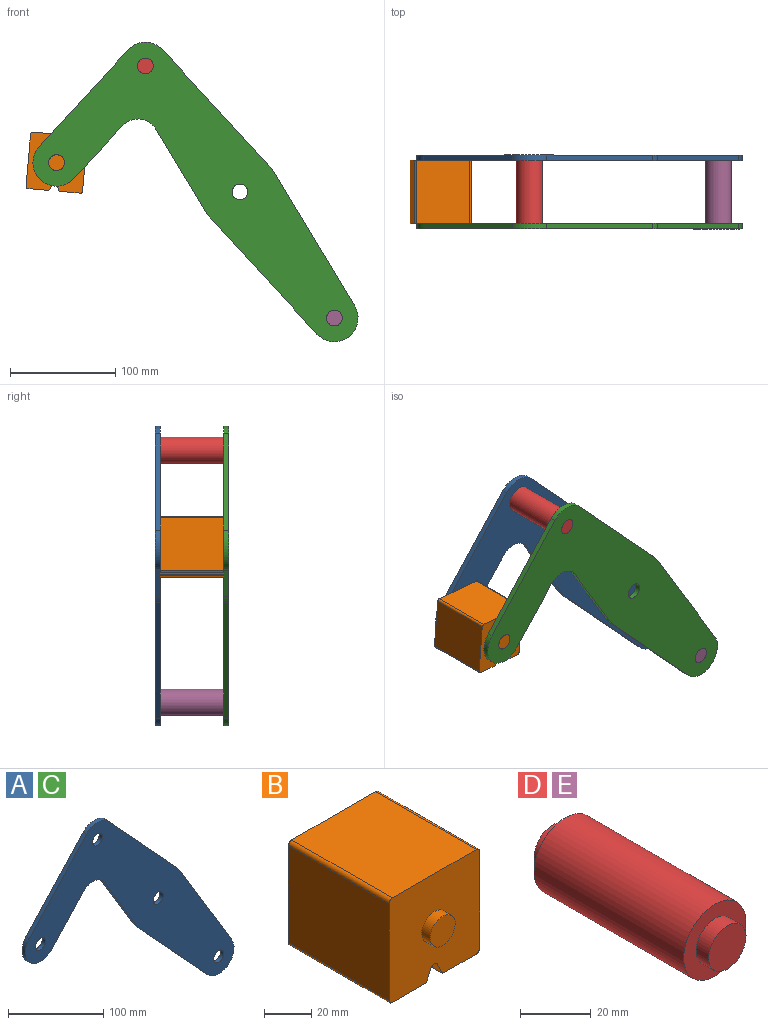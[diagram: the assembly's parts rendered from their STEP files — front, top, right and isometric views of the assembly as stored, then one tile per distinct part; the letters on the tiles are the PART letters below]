
ASSEMBLY  parts=5 mates=3
PART A: 18 faces, bbox 309.5x5x285.1 mm
  f0: cylinder r=22.5mm len=39.07mm, axis (0,1,0), area 353.4mm2, adj f1,f13,f16,f17
  f1: plane 50.28x46.21mm, normal (0.74,0,-0.68), area 341.4mm2, adj f0,f2,f16,f17
  f2: cylinder r=20mm len=31.85mm, axis (0,1,0), area 185.5mm2, adj f1,f3,f16,f17
  f3: plane 79.23x47.81mm, normal (-0.86,0,-0.52), area 462.7mm2, adj f2,f4,f16,f17
  f4: cylinder r=37.5mm len=6mm, axis (0,1,0), area 37.6mm2, adj f3,f5,f16,f17
  f5: plane 109.88x101mm, normal (-0.74,0,-0.68), area 746.2mm2, adj f4,f6,f16,f17
  f6: cylinder r=22.5mm len=39.07mm, axis (0,1,0), area 330.9mm2, adj f5,f7,f16,f17
  f7: plane 127.78x77.11mm, normal (0.86,0,0.52), area 746.2mm2, adj f6,f8,f16,f17
  f8: cylinder r=37.5mm len=6mm, axis (0,1,0), area 37.6mm2, adj f7,f9,f16,f17
  f9: plane 109.88x101mm, normal (0.74,0,0.68), area 746.2mm2, adj f8,f10,f16,f17
  f10: cylinder r=22.5mm len=33.13mm, axis (0,1,0), area 186.2mm2, adj f9,f13,f16,f17
  f11: cylinder r=7.5mm len=15mm, axis (0,1,0), area 235.6mm2, adj f16,f17
  f12: cylinder r=7.5mm len=15mm, axis (0,1,0), area 235.6mm2, adj f16,f17
  f13: plane 92.03x84.59mm, normal (-0.74,0,0.68), area 625mm2, adj f0,f10,f16,f17
  f14: cylinder r=7.5mm len=15mm, axis (0,1,0), area 235.6mm2, adj f16,f17
  f15: cylinder r=7.5mm len=15mm, axis (0,1,0), area 235.6mm2, adj f16,f17
  f16: plane 309.5x285.07mm, normal (0,-1,0), area 24555.4mm2, adj f0,f1,f2,f3,f4,f5,f6,f7
  f17: plane 309.5x285.07mm, normal (0,1,0), area 24555.4mm2, adj f0,f1,f2,f3,f4,f5,f6,f7
PART B: 18 faces, bbox 54x70x54 mm
  f0: plane 60x50.01mm, normal (0,0,1), area 3000.4mm2, adj f4,f10,f13,f14
  f1: plane 60x50.01mm, normal (-1,0,0), area 3000.4mm2, adj f4,f10,f14,f15
  f2: plane 60x20mm, normal (0,0,-1), area 1200.2mm2, adj f3,f4,f10,f15
  f3: plane 60x6.42mm, normal (0.89,0,-0.45), area 430.8mm2, adj f2,f4,f10,f16
  f4: plane 54.01x54.01mm, normal (0,-1,0), area 2690.1mm2, adj f0,f1,f2,f3,f5,f6,f7,f9
  f5: plane 60x50.01mm, normal (1,0,0), area 3000.4mm2, adj f4,f10,f13,f17
  f6: plane 60x6.42mm, normal (-0.89,0,-0.45), area 430.8mm2, adj f4,f7,f10,f16
  f7: plane 60x20mm, normal (0,0,-1), area 1200.2mm2, adj f4,f6,f10,f17
  f8: plane 15x15mm, normal (0,-1,0), area 176.7mm2, adj f9
  f9: cylinder r=7.5mm len=15mm, axis (0,1,0), area 235.6mm2, adj f4,f8
  f10: plane 54.01x54.01mm, normal (0,1,0), area 2690.1mm2, adj f0,f1,f2,f3,f5,f6,f7,f12
  f11: plane 15x15mm, normal (0,1,0), area 176.7mm2, adj f12
  f12: cylinder r=7.5mm len=15mm, axis (0,-1,0), area 235.6mm2, adj f10,f11
  f13: cylinder r=2mm len=60mm, axis (0,-1,0), area 188.5mm2, adj f0,f4,f5,f10
  f14: cylinder r=2mm len=60mm, axis (0,1,0), area 188.5mm2, adj f0,f1,f4,f10
  f15: cylinder r=2mm len=60mm, axis (0,-1,0), area 188.5mm2, adj f1,f2,f4,f10
  f16: cylinder r=2mm len=60mm, axis (0,-1,0), area 265.7mm2, adj f3,f4,f6,f10
  f17: cylinder r=2mm len=60mm, axis (0,1,0), area 188.5mm2, adj f4,f5,f7,f10
PART C: same geometry as A
PART D: 7 faces, bbox 25x70x25 mm
  f0: cylinder r=12.5mm len=60mm, axis (0,-1,0), area 4712.4mm2, adj f2,f5
  f1: cylinder r=7.5mm len=15mm, axis (0,1,0), area 235.6mm2, adj f2,f3
  f2: plane 25x25mm, normal (0,-1,0), area 314.2mm2, adj f0,f1
  f3: plane 15x15mm, normal (0,-1,0), area 176.7mm2, adj f1
  f4: cylinder r=7.5mm len=15mm, axis (0,-1,0), area 235.6mm2, adj f5,f6
  f5: plane 25x25mm, normal (0,1,0), area 314.2mm2, adj f0,f4
  f6: plane 15x15mm, normal (0,1,0), area 176.7mm2, adj f4
PART E: same geometry as D
PLACE A t=(0,35,0)mm
PLACE B rot(axis=(0,1,0),5deg) t=(-3.1,-30,-15.11)mm
PLACE C t=(0,-30,0)mm fixed
PLACE D t=(0,-30,0)mm
PLACE E t=(179.91,-30,-240.07)mm
MATE fastened A.f10 <-> D.f0  axis (0,-1,0) through (-89.96,30,120.03)mm
MATE revolute C.f0 <-> B.f9  axis (0,1,0) through (-174.54,-30,28)mm
MATE fastened C.f6 <-> E.f0  axis (0,1,0) through (89.96,-30,-120.03)mm
